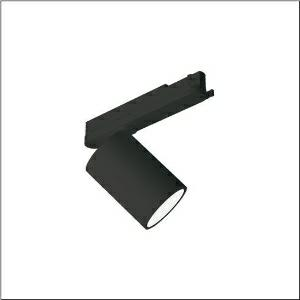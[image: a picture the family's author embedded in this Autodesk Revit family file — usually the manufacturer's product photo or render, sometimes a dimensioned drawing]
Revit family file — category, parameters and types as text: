
# Revit family: spot_31_51sf33mab4b
name_source: partatom
category: Lighting Fixtures
units: mm (PartAtom-declared; Revit-internal decimal feet)

## family parameters
Cut with Voids When Loaded = No
Host = Face
Light Source = No
Part Type = Normal
Room Calculation Point = No
Round Connector Dimension = Use Diameter
Shared = No

## types (1)
- --- (1 x LED, 5030 lm, 41.7 W, 3000K)
    Apparent Load = 42 VA
    CIE Flux Codes = 92 97 99 100 100
    Color Rendering = 90
    Color Temperature = 3000K
    Default Elevation = 1800 mm
    Description = Spot 31, directional spotlight, light control with lens, of PMMA, LED rated luminous flux: 4.830lm, light colour: 930, control gear: ECG Multilumen, with 3-phase adapter, mains connection: 220..240V, AC, 50/60Hz, of aluminium, jet black (RAL 9005), length: 213mm, diameter: 90mm, protection rating (complete): IP20, insulation class (complete): insulation class I (protective earthing), certification: CE, impact resistance: IK02, permissible ambient temperature for indoor applications: -20..+40°C, packaging unit: 1 piece
    Height = 175 mm
    Lamp = 1 x LED
    Lamp Light Flux = 5030 lm
    Lamp Power = 41.7 W
    Lamp count = 1
    Length = 90 mm
    Luminous efficacy = 121 lm/W
    Manufacturer = Siteco
    ModVariant = No
    Model = 51SF33MAB4B
    Mounting Place = Ceiling
    Mounting Type = Pendant
    Number of Poles = 1
    OnlyDefault = Yes
    Power Factor = 1
    Product Name = Spot 31
    Product group = directional spotlight
    ProductGroupID = 906
    Protection Class = Protection class I
    Protection Degree = IP 20
    RLX_Detail_Level = 1
    RLX_Emergency_Light_Flux = 0 lm
    RLX_Emergency_Type = 0
    RLX_Emergency_Type_DB = No
    RlxData = <blob elided: 20889 chars, md5=dbc67c01>
    Socket = socket
    Standby Power = 0 W
    System Light Flux = 5030 lm
    System Power = 42 W
    Type Comments = factory setting: luminous flux: 100 % | (ON | ON | ON | ON) | 1050 mA
    Type Image = l_1273723.jpg
    URL = http://relux.com
    VarID = @adj_146442
    Voltage = 0 V
    Weight = 0.00 kg
    Width = 0 mm  [stored 0 ft]

note: [stored X ft] marks values corroborated as IEEE doubles in the binary element streams (Revit-internal decimal feet)

## geometry (parser evidence)
native form markers: Blend x4, Sweep x11
no freeform markers — native parametric forms only
